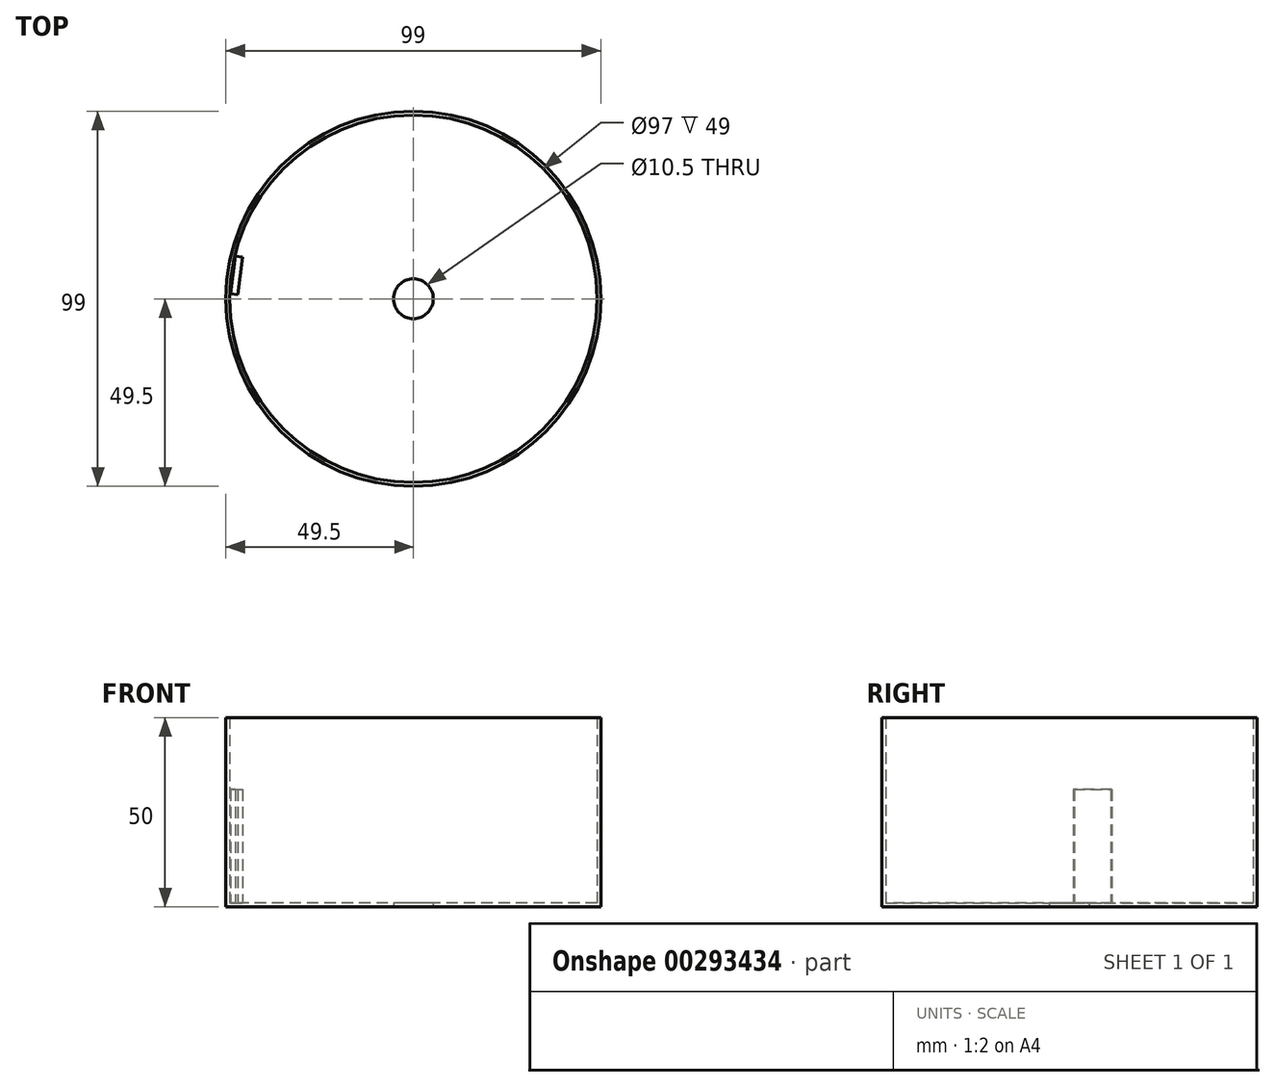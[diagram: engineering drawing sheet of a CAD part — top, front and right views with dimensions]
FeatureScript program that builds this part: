
annotation { "Feature Type Name" : "Feature", "Feature Type Description" : "" }
export const myFeature = defineFeature(function(context is Context, id is Id, definition is map)
    precondition{}
    {
        {
            var Q0;
            Q0=qCreatedBy(makeId("Top.planeOp"),FACE);
            var sketch = newSketch(context, id + "F0", { "sketchPlane" : qUnion([Q0])});
            skCircle(sketch, "E0", {"center": v(0, 0) * mm, "radius": 49.5 * mm});
            skCircle(sketch, "E1", {"center": v(0, 0) * mm, "radius": 48.5 * mm});
            skCircle(sketch, "E2", {"center": v(0, 0) * mm, "radius": 5.25 * mm});
            skSolve(sketch);
        }
        {
            var Q0;
            Q0=makeQuery(id+"F0.imprint","IMPRINT",FACE,{"disambiguationData":[TD([[makeQuery(id+"F0.imprint","IMPRINT",EDGE,{"derivedFrom":sQuery(id+"F0.wireOp",EDGE,"E0")}),1.0]])]});
            extrude(context, id + "F1", {"entities" : qUnion([Q0]), "depth" : 50 * mm});
        }
        {
            var Q0;
            Q0=makeQuery(id+"F0.imprint","IMPRINT",FACE,{"disambiguationData":[TD([[makeQuery(id+"F0.imprint","IMPRINT",EDGE,{"derivedFrom":sQuery(id+"F0.wireOp",EDGE,"E1")}),1.0]])]});
            extrude(context, id + "F2", {"entities" : qUnion([Q0]), "operationType" : NewBodyOperationType.ADD, "depth" : 1 * mm});
        }
        {
            var Q0;
            Q0=makeQuery(id+"F2.opExtrude","CAP_FACE",FACE,{"disambiguationData":[OSD([sQuery(id+"F0.wireOp",EDGE,"E1")])],"isStart":false});
            var sketch = newSketch(context, id + "F3", { "sketchPlane" : qUnion([Q0])});
            skLineSegment(sketch, "E3", {"start": v(-53.1, -14.23) * mm, "end": v(72.24, 19.36) * mm});
            skLineSegment(sketch, "E4", {"start": v(-27.61, 47.83) * mm, "end": v(34.9, -60.44) * mm});
            skLineSegment(sketch, "E5", {"start": v(-55.46, 0) * mm, "end": v(58.15, 0) * mm});
            skLineSegment(sketch, "E6", {"start": v(0, 55.24) * mm, "end": v(0, -52.4) * mm});
            skLineSegment(sketch, "E7", {"start": v(-49.34, -28.49) * mm, "end": v(47.4, 27.36) * mm});
            skLineSegment(sketch, "E8", {"start": v(-53.87, 14.43) * mm, "end": v(52.36, -14.03) * mm});
            skLineSegment(sketch, "E9", {"start": v(17.4, -64.95) * mm, "end": v(-17.3, 64.59) * mm});
            skLineSegment(sketch, "E10", {"start": v(-58.27, 33.64) * mm, "end": v(55.8, -32.22) * mm});
            skLineSegment(sketch, "E11", {"start": v(-48.3, 48.3) * mm, "end": v(52.81, -52.81) * mm});
            skLineSegment(sketch, "E12", {"start": v(-40.63, -40.63) * mm, "end": v(40.64, 40.64) * mm});
            skLineSegment(sketch, "E13", {"start": v(14.84, 55.39) * mm, "end": v(-17.74, -66.2) * mm});
            skLineSegment(sketch, "E14", {"start": v(-31.98, -55.39) * mm, "end": v(33.55, 58.11) * mm});
            skLineSegment(sketch, "E15", {"start": v(-46.85, 12.55) * mm, "end": v(-48.5, 0) * mm});
            skLineSegment(sketch, "E16", {"start": v(-48.5, 0) * mm, "end": v(-46.52, -0.26) * mm});
            skLineSegment(sketch, "E17", {"start": v(-46.52, -0.26) * mm, "end": v(-44.86, 12.3) * mm});
            skLineSegment(sketch, "E18", {"start": v(-44.86, 12.3) * mm, "end": v(-46.85, 12.55) * mm});
            skLineSegment(sketch, "E19", {"start": v(-47.67, 6.28) * mm, "end": v(-45.7, 6.02) * mm});
            skLineSegment(sketch, "E20", {"start": v(-47.02, 11.23) * mm, "end": v(-45.04, 10.97) * mm});
            skLineSegment(sketch, "E21", {"start": v(-48.33, 1.32) * mm, "end": v(-46.34, 1.06) * mm});
            skSolve(sketch);
        }
        {
            var Q0;
            {var subQ0=sQuery(id+"F3.wireOp",EDGE,"E19");Q0=makeQuery(id+"F3.imprint","IMPRINT",FACE,{"disambiguationData":[TD([[makeQuery(id+"F3.imprint","IMPRINT",EDGE,{"derivedFrom":subQ0}),1.0]])]});}
            var Q1;
            {var subQ0=sQuery(id+"F3.wireOp",EDGE,"E19");Q1=makeQuery(id+"F3.imprint","IMPRINT",FACE,{"disambiguationData":[TD([[makeQuery(id+"F3.imprint","IMPRINT",EDGE,{"derivedFrom":subQ0}),-1.0]])]});}
            extrude(context, id + "F4", {"entities" : qUnion([Q0, Q1]), "operationType" : NewBodyOperationType.ADD, "depth" : 30 * mm});
        }
    });
